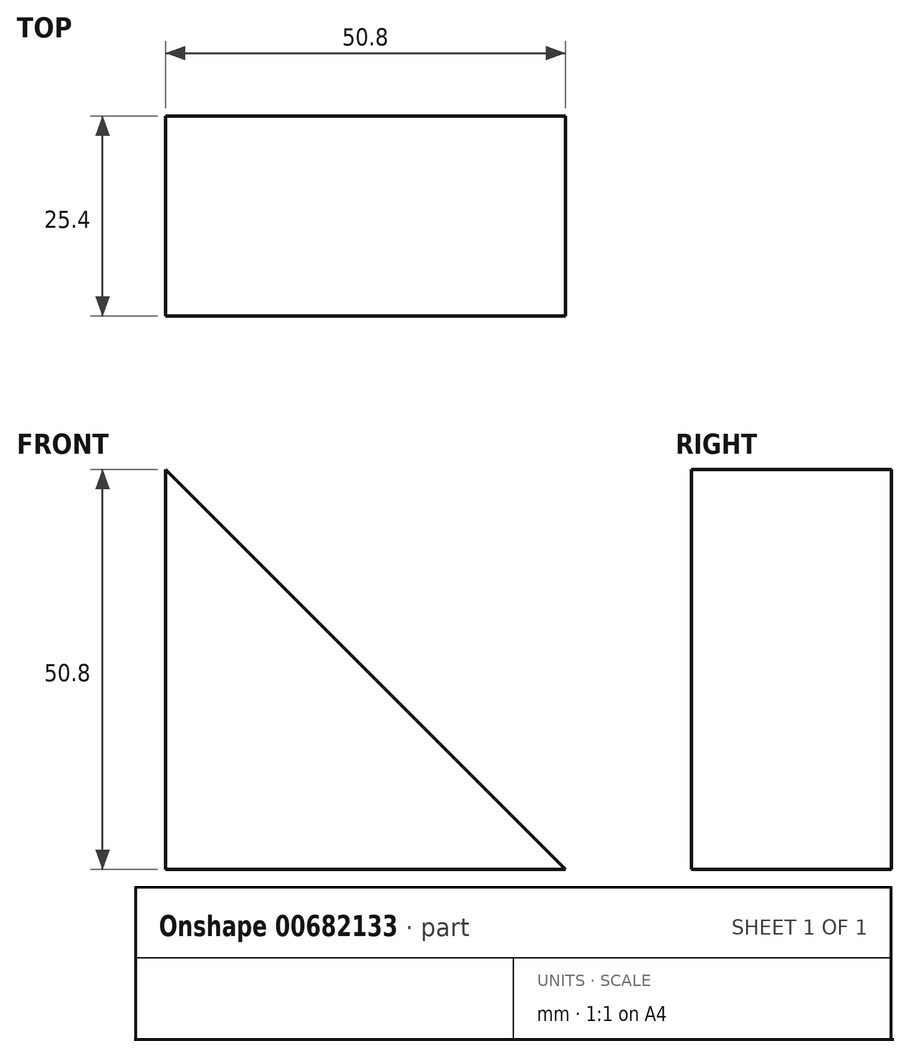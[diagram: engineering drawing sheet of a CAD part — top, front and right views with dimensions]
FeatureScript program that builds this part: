
annotation { "Feature Type Name" : "Feature", "Feature Type Description" : "" }
export const myFeature = defineFeature(function(context is Context, id is Id, definition is map)
    precondition{}
    {
        {
            var Q0;
            Q0=qCreatedBy(makeId("Front.planeOp"),FACE);
            var sketch = newSketch(context, id + "F0", { "sketchPlane" : qUnion([Q0])});
            skLineSegment(sketch, "E0", {"start": v(-23.47, 69.2) * mm, "end": v(-23.47, 18.4) * mm});
            skLineSegment(sketch, "E1", {"start": v(-23.47, 18.4) * mm, "end": v(27.33, 18.4) * mm});
            skLineSegment(sketch, "E2", {"start": v(27.33, 18.4) * mm, "end": v(-23.47, 69.2) * mm});
            skSolve(sketch);
        }
        {
            var Q0;
            Q0 = qSketchRegion(id + "F0", true);
            extrude(context, id + "F1", {"entities" : qUnion([Q0]), "depth" : 25.4 * mm, "offsetDistance" : 25.4 * mm});
        }
    });
